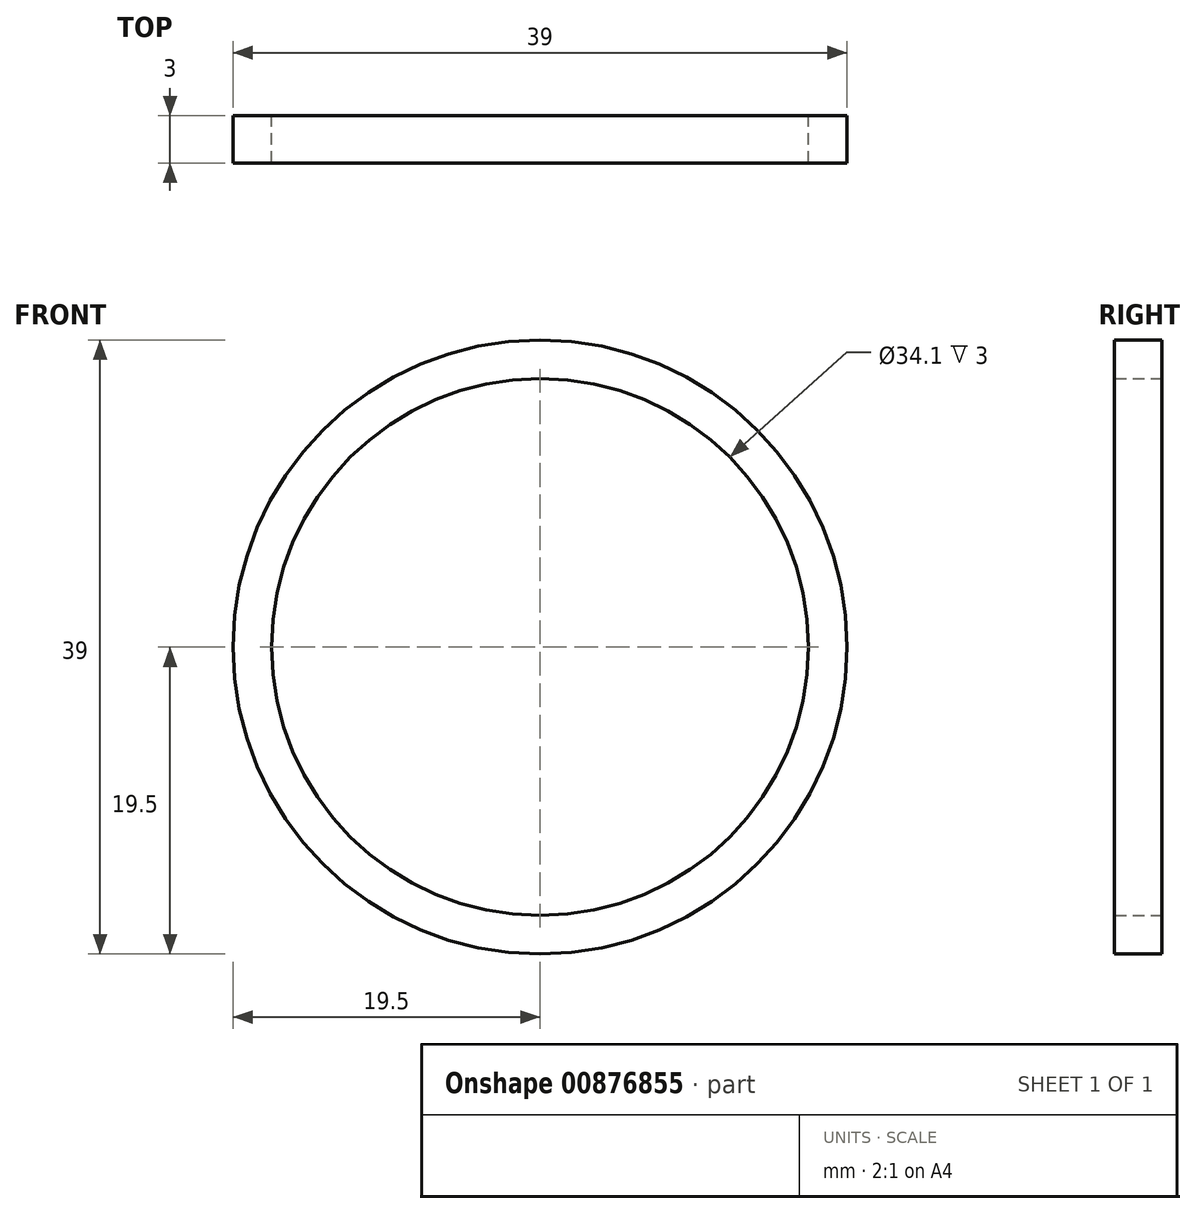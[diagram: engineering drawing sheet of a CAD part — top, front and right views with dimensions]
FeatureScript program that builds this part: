
annotation { "Feature Type Name" : "Feature", "Feature Type Description" : "" }
export const myFeature = defineFeature(function(context is Context, id is Id, definition is map)
    precondition{}
    {
        {
            var Q0;
            Q0=qCreatedBy(makeId("Front.planeOp"),FACE);
            var sketch = newSketch(context, id + "F0", { "sketchPlane" : qUnion([Q0])});
            skCircle(sketch, "E0", {"center": v(0, 0) * mm, "radius": 19.5 * mm});
            skCircle(sketch, "E1", {"center": v(0, 0) * mm, "radius": 17.05 * mm});
            skSolve(sketch);
        }
        {
            var Q0;
            Q0=makeQuery(id+"F0.imprint","IMPRINT",FACE,{"disambiguationData":[TD([[makeQuery(id+"F0.imprint","IMPRINT",EDGE,{"derivedFrom":sQuery(id+"F0.wireOp",EDGE,"E0")}),1.0]])]});
            extrude(context, id + "F1", {"entities" : qUnion([Q0]), "depth" : 3 * mm, "offsetDistance" : 25 * mm});
        }
    });
